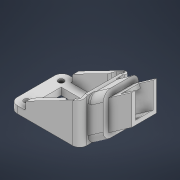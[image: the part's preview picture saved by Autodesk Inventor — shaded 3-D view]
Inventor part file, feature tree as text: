
AUTODESK INVENTOR PART (.ipt)
format: ipt  version: 2021 (Build 250183000, 183)  size: 695,808 bytes
history: native  units: mm
features: sketch x14, extrude x13, plane x7, fillet x7, other x1, shell x1
ambient origin geometry x8: Origin, YZ Plane, XZ Plane, XY Plane, X Axis, Y Axis, Z Axis, Center Point
bodies: Volumenkörper1 (feature_tree)
feature tree (43):
  other  "Servohalterung"
  plane  "Arbeitsebene2"
  sketch  "Skizze4"  dims[d34=20.0mm d35=24.415mm]
  plane  "Arbeitsebene3"
  extrude  "Extrusion9"  Depth=24.415mm
  plane  "Arbeitsebene5"
  extrude  "Extrusion10"  Depth=4.0mm TaperAngle=0.0deg
  plane  "Arbeitsebene1"
  extrude  "Extrusion18"  Depth=10.0mm
  shell  "Wandung6"  Thickness=24.415mm
  plane  "Arbeitsebene6"
  extrude  "Extrusion19"  Depth=6.108652mm
  plane  "Arbeitsebene4"
  extrude  "Extrusion21"  Depth=4.0mm
  extrude  "Extrusion22"  Depth=14.0mm TaperAngle=0.0deg
  extrude  "Extrusion23"  TaperAngle=0.0deg  [1 undecoded]
  extrude  "Extrusion24"  Depth=10.0mm
  extrude  "Extrusion25"  Depth=4.0mm
  fillet  "Rundung9"  Radius=39.5mm
  fillet  "Rundung10"  Radius=4.0mm
  plane  "Arbeitsebene7"
  extrude  "Extrusion26"  Depth=3.0mm TaperAngle=0.0deg
  extrude  "Extrusion27"  Depth=3.5mm TaperAngle=0.0deg
  extrude  "Extrusion28"  Depth=4.0mm
  fillet  "Rundung11"  Radius=4.0mm
  extrude  "Extrusion29"  Depth=4.0mm
  fillet  "Rundung12"  Radius=4.0mm
  fillet  "Rundung13"  Radius=22.0mm
  fillet  "Rundung14"  Radius=8.0mm
  fillet  "Rundung15"  Radius=8.0mm
  sketch  "Skizze10"  dims[d36=0.0mm d37=4.0mm d38=0.0mm]
  sketch  "Skizze11"  dims[d39=10.0mm d40=6.108652mm d42=24.415mm]
  sketch  "Skizze21"  dims[d43=20.0mm d44=0.0mm d92=6.108652mm]
  sketch  "Skizze22"  dims[d98=17.091mm d100=4.0mm]
  sketch  "Skizze24"  dims[d107=17.091mm d108=14.0mm d109=0.0mm]
  sketch  "Skizze25"  dims[d110=2.0mm d111=0.0mm]
  sketch  "Skizze26"  dims[d112=0.0mm d113=10.0mm]
  sketch  "Skizze28"  dims[d114=3.0mm d115=0.0mm d121=29.5mm d122=39.5mm d124=4.0mm d125=0.0mm]
  sketch  "Skizze31"  dims[d126=18.415mm d127=0.0mm d128=3.0mm d129=0.0mm]
  sketch  "Skizze32"  dims[d130=3.0mm d131=0.0mm d132=3.5mm d133=0.0mm]
  sketch  "Skizze34"  dims[d134=4.0mm d135=4.0mm d136=4.0mm]
  sketch  "Skizze35"  dims[d137=8.0mm d138=8.0mm d139=4.0mm d140=22.0mm d141=0.0mm d142=8.0mm d143=8.0mm]
  sketch  "Skizze36"  dims[d144=4.0mm d145=4.0mm d146=22.0mm d147=0.0mm d148=0.0mm d149=0.0mm d150=1.0mm d151=0.0mm d152=2.0mm d153=9.0mm d154=9.0mm d155=4.5mm d156=4.0mm d161=5.0mm d162=0.0mm d166=9.0mm d167=9.0mm d170=4.5mm d171=4.0mm d172=1.0mm d173=1.0mm d174=4.0mm d175=4.0mm d46=0.5mm d47=0.872665mm d48=0.5mm d49=0.872665mm d59=0.5mm d60=0.872665mm d61=0.5mm d62=0.872665mm]
note: 1 required parameter value undecoded (feature->parameter linkage not recoverable at this tier; creation-order binding heuristic only, values carry confidence <= 0.55)
